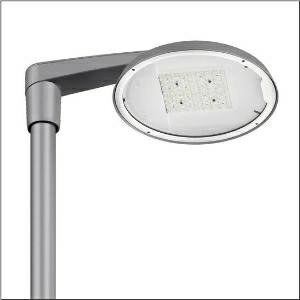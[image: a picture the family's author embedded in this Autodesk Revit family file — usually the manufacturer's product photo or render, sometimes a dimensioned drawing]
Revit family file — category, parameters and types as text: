
# Revit family: dl_r__50_iq_mini___st0_5a_5xa248b31f08me_0590
name_source: partatom
category: Lighting Fixtures
units: mm (PartAtom-declared; Revit-internal decimal feet)

## family parameters
Cut with Voids When Loaded = No
Host = Face
Light Source = No
Part Type = Normal
Room Calculation Point = No
Round Connector Dimension = Use Diameter
Shared = No

## types (1)
- --- (1 x LED, 15660 lm, 107.8 W, 3000K)
    Apparent Load = 108 VA
    CIE Flux Codes = 41 75 97 100 100
    Color Rendering = 70
    Color Temperature = 3000K
    Default Elevation = 1800 mm
    Description = DL® 50 iQ mini, mast luminaire, primary light control with lens, of PMMA, primary optical cover: cover, of toughened safety glass, transparent, light distribution: ST0.5a, light emission: direct distribution, primary light characteristic: asymmetric, installation type: side-entry, post-top, LED, High Power LED, rated luminous flux: 15.660lm, luminous efficacy: 145lm/W, light colour: 730, colour temperature: 3000K, control gear: iQ Street-Remote, control: optimised constant luminous flux control (CLO 2.0), Desk-Remote (wireless, voltage-free reading and setting of iQ features in the workshop via application-optimized NFC function/RFID function), Light-Fading, Smart-Wire, Night-Set, Lumen-Switch, Temp-Guard, Auto-Match, Street-Remote, mains connection: 230..240V, AC, 50/60Hz, connection cable pre-assembled, cable length: 10,5m, start of lifetime: 108W, end of service life: 118W, reduction: 47W, luminaire housing, of diecast aluminium, powder-coated, Siteco® metallic grey (DB 702S), inclination adjustable: 0°, 5°, 10° (post-top) | 0°, -5°, -10°, -15° (side-entry), please order mast post-top element or mast side-entry element separately, diameter: 500mm, height: 115mm, post-top: for spigot size d x l = 76 x 100mm; with reducer (optional accessory) 60 x 100mm | side-entry: for spigot size d x l = 60 x 100mm; with reducer (optional accessory) 42 x 100mm, mounting height: 4..6m, protection rating (complete): IP66, insulation class (complete): insulation class II (safety insulation), certification: CE, ENEC, ENEC+, VDE, impact resistance: IK08, permissible operating ambient temperature for outdoor applications: -25..+40°C, standard-compliant lighting for roads and squares, packaging unit: 1 piece

Light Distribution: ST0.5a
    Height = 115 mm
    Lamp = 1 x LED
    Lamp Light Flux = 15660 lm
    Lamp Power = 107.8 W
    Lamp count = 1
    Length = 500 mm
    Luminous efficacy = 145 lm/W
    Manufacturer = Siteco
    ModVariant = No
    Model = 5XA248B31F08ME
    Number of Poles = 1
    OnlyDefault = Yes
    Power Factor = 1
    Product Name = DL® 50 iQ mini | ST0.5a
    Product group = mast luminaire | pylon top
    ProductGroupID = 6100
    Protection Class = Protection class II
    Protection Degree = IP 66
    RLX_Detail_Level = 1
    RLX_Emergency_Light_Flux = 0 lm
    RLX_Emergency_Type = 0
    RLX_Emergency_Type_DB = No
    RlxData = <blob elided: 128061 chars, md5=af9dc94c>
    Socket = socket
    Standby Power = 0 W
    System Light Flux = 15660 lm
    System Power = 108 W
    Type Comments = factory setting: luminous flux: 100 % | dim-lin: 254 | 565 mA
    Type Image = l_1251790.jpg
    URL = http://relux.com
    VarID = @adj_164551
    Voltage = 0 V
    Weight = 0.00 kg
    Width = 0 mm  [stored 0 ft]

note: [stored X ft] marks values corroborated as IEEE doubles in the binary element streams (Revit-internal decimal feet)

## geometry (parser evidence)
native form markers: Blend x4, Sweep x11
no freeform markers — native parametric forms only
